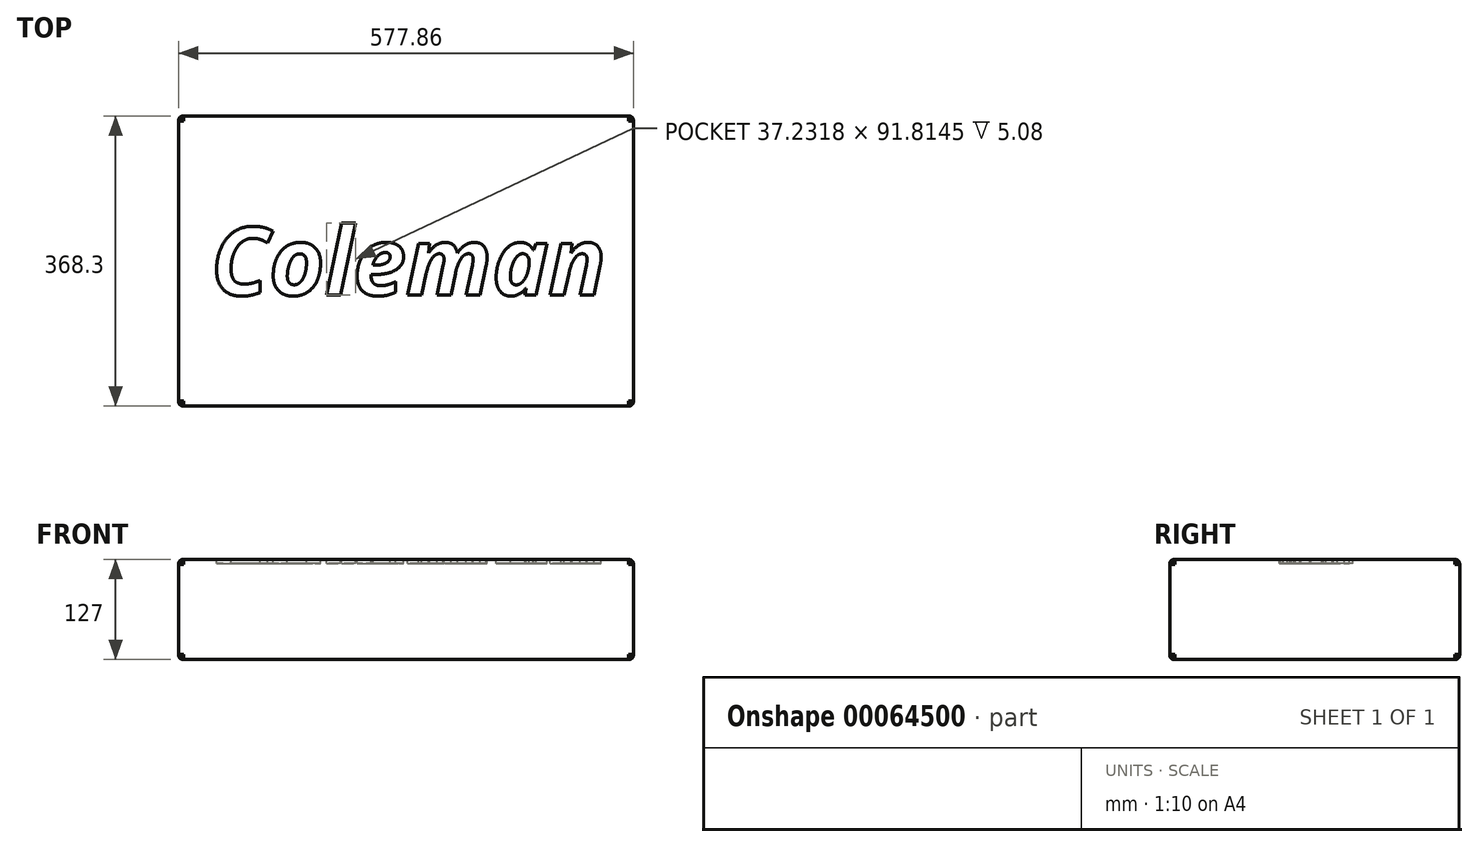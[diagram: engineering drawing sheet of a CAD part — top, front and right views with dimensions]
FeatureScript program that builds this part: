
annotation { "Feature Type Name" : "Feature", "Feature Type Description" : "" }
export const myFeature = defineFeature(function(context is Context, id is Id, definition is map)
    precondition{}
    {
        {
            var Q0;
            Q0=qCreatedBy(makeId("Top.planeOp"),FACE);
            var sketch = newSketch(context, id + "F0", { "sketchPlane" : qUnion([Q0])});
            skLineSegment(sketch, "E0.rect.bottom", {"start": v(288.93, -184.15) * mm, "end": v(-288.93, -184.15) * mm});
            skLineSegment(sketch, "E0.rect.top", {"start": v(288.93, 184.15) * mm, "end": v(-288.93, 184.15) * mm});
            skLineSegment(sketch, "E0.rect.left", {"start": v(288.93, -184.15) * mm, "end": v(288.93, 184.15) * mm});
            skLineSegment(sketch, "E0.rect.right", {"start": v(-288.93, -184.15) * mm, "end": v(-288.93, 184.15) * mm});
            skPoint(sketch, "E0.rect.middle", {"position": v(0, 0) * mm});
            skSolve(sketch);
        }
        {
            var Q0;
            Q0=makeQuery(id+"F0.imprint","IMPRINT",FACE,{"disambiguationData":[TD([[makeQuery(id+"F0.imprint","IMPRINT",EDGE,{"derivedFrom":sQuery(id+"F0.wireOp",EDGE,"E0.rect.bottom")}),-1.0]])]});
            extrude(context, id + "F1", {"entities" : qUnion([Q0]), "depth" : 127 * mm});
        }
        {
            var Q0;
            Q0=makeQuery(id+"F1.opExtrude","SWEPT_FACE",FACE,{"disambiguationData":[OSD([sQuery(id+"F0.wireOp",EDGE,"E0.rect.bottom")])]});
            var Q1;
            Q1=makeQuery(id+"F1.opExtrude","SWEPT_FACE",FACE,{"disambiguationData":[OSD([sQuery(id+"F0.wireOp",EDGE,"E0.rect.left")])]});
            var Q2;
            Q2=makeQuery(id+"F1.opExtrude","SWEPT_FACE",FACE,{"disambiguationData":[OSD([sQuery(id+"F0.wireOp",EDGE,"E0.rect.top")])]});
            var Q3;
            Q3=makeQuery(id+"F1.opExtrude","SWEPT_FACE",FACE,{"disambiguationData":[OSD([sQuery(id+"F0.wireOp",EDGE,"E0.rect.right")])]});
            fillet(context, id + "F2", {"entities" : qUnion([Q0, Q1, Q2, Q3]), "radius" : 6.35 * mm, "tangentPropagation" : true, "rho" : 0.5, "crossSection" : FilletCrossSection.CONIC, "allowEdgeOverflow" : false});
        }
        {
            var Q0;
            Q0=makeQuery(id+"F1.opExtrude","CAP_FACE",FACE,{"disambiguationData":[OSD([sQuery(id+"F0.wireOp",EDGE,"E0.rect.bottom"),sQuery(id+"F0.wireOp",EDGE,"E0.rect.top"),sQuery(id+"F0.wireOp",EDGE,"E0.rect.left"),sQuery(id+"F0.wireOp",EDGE,"E0.rect.right")])],"isStart":false});
            var sketch = newSketch(context, id + "F3", { "sketchPlane" : qUnion([Q0])});
            skLineSegment(sketch, "E1.rect.bottom", {"start": v(247.89, -43.5) * mm, "end": v(-247.89, -43.5) * mm, "construction": true});
            skLineSegment(sketch, "E1.rect.top", {"start": v(247.89, 43.5) * mm, "end": v(-247.89, 43.5) * mm, "construction": true});
            skLineSegment(sketch, "E1.rect.left", {"start": v(247.89, -43.5) * mm, "end": v(247.89, 43.5) * mm, "construction": true});
            skLineSegment(sketch, "E1.rect.right", {"start": v(-247.89, -43.5) * mm, "end": v(-247.89, 43.5) * mm, "construction": true});
            skPoint(sketch, "E1.rect.middle", {"position": v(0, 0) * mm});
            skText(sketch, "E2", { "text": "Coleman", "fontName": "OpenSans-BoldItalic.ttf"});
            const initialGuessF3  = {"E2": [-0.24789, -0.0435, 1, 0, 0.087]};
            skSetInitialGuess(sketch, initialGuessF3);
            skSolve(sketch);
        }
        {
            var Q0;
            Q0 = qSketchRegion(id + "F3", true);
            extrude(context, id + "F4", {"entities" : qUnion([Q0]), "operationType" : NewBodyOperationType.REMOVE, "oppositeDirection" : true, "depth" : 5.08 * mm});
        }
    });
